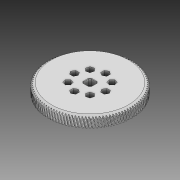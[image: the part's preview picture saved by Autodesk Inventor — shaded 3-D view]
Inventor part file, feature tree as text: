
AUTODESK INVENTOR PART (.ipt)
format: ipt  version: 2020 (Build 240168000, 168)  size: 1,517,568 bytes
history: native  units: mm
features: sketch x4, extrude x3, other x2, chamfer x2, revolve x1
ambient origin geometry x8: Origin, YZ Plane, XZ Plane, XY Plane, X Axis, Y Axis, Z Axis, Center Point
bodies: Solid1 (feature_tree)
feature tree (12):
  sketch  "Sketch1"  dims[d8=5.0mm d11=6.0mm]
  revolve  "Revolution1"  [1 undecoded]
  extrude  "Extrusion1"  Depth=10.0mm
  extrude  "Extrusion2"  Depth=8.0mm
  extrude  "Extrusion3"  Depth=10.0mm
  other  "Spur Gear Teeth1"
  chamfer  "Chamfer1"  Distance=80.0mm Angle=360.0deg
  chamfer  "Chamfer2"  [1 undecoded]
  sketch  "Sketch2"  dims[d13=10.0mm d15=54.0mm]
  sketch  "Sketch3"  dims[d16=90.0deg d21=8.0mm]
  sketch  "Sketch4"  dims[d22=20.0mm d23=5.5mm d24=80.0mm d26=360.0deg d28=0.0mm d29=0.0mm d30=8.2mm d31=80.0mm d33=360.0deg d35=6.0mm d36=0.0mm d37=6.1mm d38=8.0mm d39=0.5mm d40=2.0mm d41=45.0deg d42=27.0mm d43=3.5mm d44=3.0mm d45=24.95mm d46=10.25mm d47=10.25mm d48=10.0mm d49=0.0mm d50=34.9mm d51=0.8mm d52=47.6mm d53=0.5mm d54=21.816616mm d55=0.5mm d56=2.0mm d57=45.0deg]
  other  "Spur Gear1"
note: 2 required parameter values undecoded (feature->parameter linkage not recoverable at this tier; creation-order binding heuristic only, values carry confidence <= 0.55)